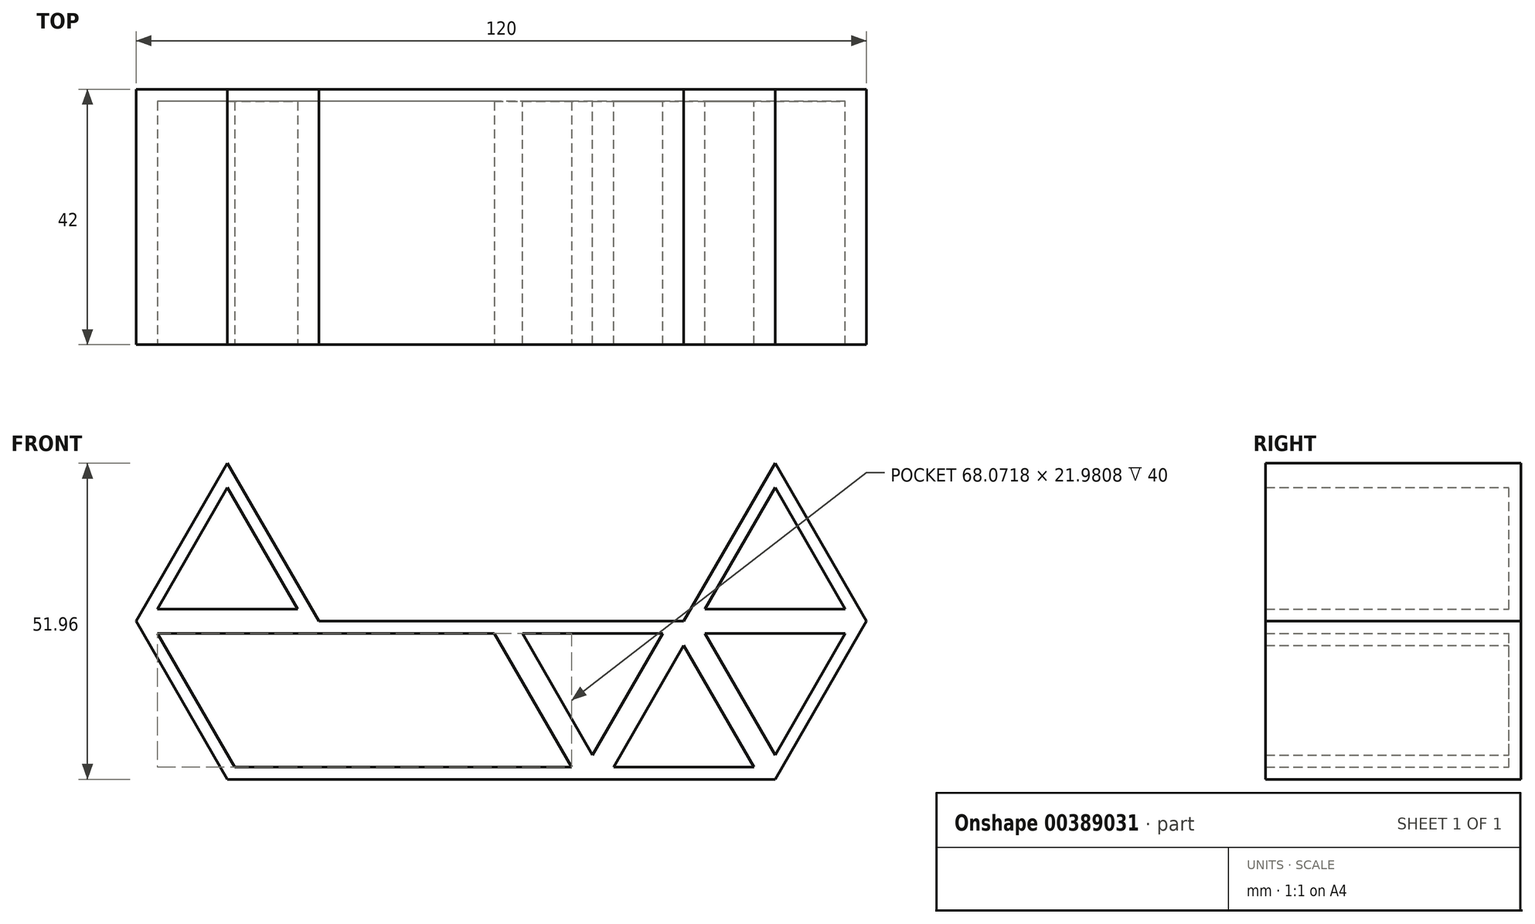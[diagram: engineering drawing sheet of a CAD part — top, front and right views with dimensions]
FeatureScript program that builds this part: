
annotation { "Feature Type Name" : "Feature", "Feature Type Description" : "" }
export const myFeature = defineFeature(function(context is Context, id is Id, definition is map)
    precondition{}
    {
        {
            var Q0;
            Q0=qCreatedBy(makeId("Front.planeOp"),FACE);
            var sketch = newSketch(context, id + "F0", { "sketchPlane" : qUnion([Q0])});
            skCircle(sketch, "E0.cCircle", {"center": v(0, 1.04) * mm, "radius": 8.66 * mm, "construction": true});
            skLineSegment(sketch, "E0.0", {"start": v(15, -7.62) * mm, "end": v(-15, -7.62) * mm});
            skLineSegment(sketch, "E0.1", {"start": v(-15, -7.62) * mm, "end": v(0, 18.36) * mm});
            skLineSegment(sketch, "E0.2", {"start": v(0, 18.36) * mm, "end": v(15, -7.62) * mm});
            skPoint(sketch, "E0.0.midPoint", {"position": v(0, -7.62) * mm});
            skLineSegment(sketch, "E1.0", {"start": v(0, 14.36) * mm, "end": v(11.54, -5.62) * mm});
            skLineSegment(sketch, "E1.1", {"start": v(-11.54, -5.62) * mm, "end": v(0, 14.36) * mm});
            skLineSegment(sketch, "E1.2", {"start": v(11.54, -5.62) * mm, "end": v(-11.54, -5.62) * mm});
            skLineSegment(sketch, "E2.MirrorCS", {"start": v(11.54, -9.62) * mm, "end": v(-11.54, -9.62) * mm});
            skCircle(sketch, "E3.MirrorC", {"center": v(0, -16.28) * mm, "radius": 8.66 * mm, "construction": true});
            skLineSegment(sketch, "E4.MirrorCS", {"start": v(-15, -7.62) * mm, "end": v(0, -33.6) * mm});
            skLineSegment(sketch, "E5.MirrorCS", {"start": v(0, -33.6) * mm, "end": v(15, -7.62) * mm});
            skLineSegment(sketch, "E6.MirrorCS", {"start": v(-11.54, -9.62) * mm, "end": v(0, -29.6) * mm});
            skLineSegment(sketch, "E7.MirrorCS", {"start": v(0, -29.6) * mm, "end": v(11.54, -9.62) * mm});
            skLineSegment(sketch, "E8.1.0.0", {"start": v(-45, -7.62) * mm, "end": v(-30, -33.6) * mm});
            skLineSegment(sketch, "E8.1.0.1", {"start": v(-15, -7.62) * mm, "end": v(-45, -7.62) * mm});
            skLineSegment(sketch, "E8.1.0.2", {"start": v(-30, -33.6) * mm, "end": v(-15, -7.62) * mm});
            skLineSegment(sketch, "E8.direction1", {"start": v(0, -33.6) * mm, "end": v(-30, -33.6) * mm, "construction": true});
            skLineSegment(sketch, "E9.0", {"start": v(-30, -29.6) * mm, "end": v(-18.46, -9.62) * mm});
            skLineSegment(sketch, "E9.1", {"start": v(-41.54, -9.62) * mm, "end": v(-30, -29.6) * mm});
            skLineSegment(sketch, "E9.2", {"start": v(-18.46, -9.62) * mm, "end": v(-41.54, -9.62) * mm});
            skLineSegment(sketch, "E10", {"start": v(-30, -33.6) * mm, "end": v(0, -33.6) * mm});
            skLineSegment(sketch, "E11.0", {"start": v(-26.54, -31.6) * mm, "end": v(-15, -11.62) * mm});
            skLineSegment(sketch, "E11.1", {"start": v(-3.46, -31.6) * mm, "end": v(-26.54, -31.6) * mm});
            skLineSegment(sketch, "E11.2", {"start": v(-15, -11.62) * mm, "end": v(-3.46, -31.6) * mm});
            skSolve(sketch);
        }
        {
            var Q0;
            Q0=makeQuery(id+"F0.imprint","IMPRINT",FACE,{"disambiguationData":[TD([[makeQuery(id+"F0.imprint","IMPRINT",EDGE,{"derivedFrom":sQuery(id+"F0.wireOp",EDGE,"E8.1.0.0")}),1.0]])]});
            var Q1;
            Q1=makeQuery(id+"F0.imprint","IMPRINT",FACE,{"disambiguationData":[TD([[makeQuery(id+"F0.imprint","IMPRINT",EDGE,{"derivedFrom":sQuery(id+"F0.wireOp",EDGE,"E4.MirrorCS")}),-1.0]])]});
            var Q2;
            Q2=makeQuery(id+"F0.imprint","IMPRINT",FACE,{"disambiguationData":[TD([[makeQuery(id+"F0.imprint","IMPRINT",EDGE,{"derivedFrom":sQuery(id+"F0.wireOp",EDGE,"E0.0")}),1.0]])]});
            var Q3;
            Q3=makeQuery(id+"F0.imprint","IMPRINT",FACE,{"disambiguationData":[TD([[makeQuery(id+"F0.imprint","IMPRINT",EDGE,{"derivedFrom":sQuery(id+"F0.wireOp",EDGE,"E0.0")}),-1.0]])]});
            extrude(context, id + "F1", {"entities" : qUnion([Q0, Q1, Q2, Q3]), "depth" : 40 * mm});
        }
        {
            var Q0;
            Q0=makeQuery(id+"F1.opExtrude","CAP_FACE",FACE,{"disambiguationData":[OSD([sQuery(id+"F0.wireOp",EDGE,"E0.1"),sQuery(id+"F0.wireOp",EDGE,"E0.2"),sQuery(id+"F0.wireOp",EDGE,"E1.0"),sQuery(id+"F0.wireOp",EDGE,"E1.1"),sQuery(id+"F0.wireOp",EDGE,"E1.2"),sQuery(id+"F0.wireOp",EDGE,"E2.MirrorCS"),sQuery(id+"F0.wireOp",EDGE,"E5.MirrorCS"),sQuery(id+"F0.wireOp",EDGE,"E6.MirrorCS"),sQuery(id+"F0.wireOp",EDGE,"E7.MirrorCS"),sQuery(id+"F0.wireOp",EDGE,"E8.1.0.0"),sQuery(id+"F0.wireOp",EDGE,"E8.1.0.1"),sQuery(id+"F0.wireOp",EDGE,"E9.0"),sQuery(id+"F0.wireOp",EDGE,"E9.1"),sQuery(id+"F0.wireOp",EDGE,"E9.2"),sQuery(id+"F0.wireOp",EDGE,"E10"),sQuery(id+"F0.wireOp",EDGE,"E11.0"),sQuery(id+"F0.wireOp",EDGE,"E11.1"),sQuery(id+"F0.wireOp",EDGE,"E11.2")])],"isStart":false});
            var sketch = newSketch(context, id + "F2", { "sketchPlane" : qUnion([Q0])});
            skLineSegment(sketch, "E12", {"start": v(-45, -7.62) * mm, "end": v(-75, -7.62) * mm});
            skLineSegment(sketch, "E13", {"start": v(-75, -7.62) * mm, "end": v(-105, -7.62) * mm});
            skLineSegment(sketch, "E14", {"start": v(-30, -33.6) * mm, "end": v(-90, -33.6) * mm});
            skLineSegment(sketch, "E15", {"start": v(-90, -33.6) * mm, "end": v(-105, -7.62) * mm});
            skLineSegment(sketch, "E16.0", {"start": v(-88.85, -31.6) * mm, "end": v(-101.54, -9.62) * mm});
            skLineSegment(sketch, "E16.1", {"start": v(-75, -9.62) * mm, "end": v(-101.54, -9.62) * mm});
            skLineSegment(sketch, "E16.2", {"start": v(-33.46, -31.6) * mm, "end": v(-88.85, -31.6) * mm});
            skLineSegment(sketch, "E16.3", {"start": v(-46.15, -9.62) * mm, "end": v(-33.46, -31.6) * mm});
            skLineSegment(sketch, "E16.4", {"start": v(-46.15, -9.62) * mm, "end": v(-75, -9.62) * mm});
            skSolve(sketch);
        }
        {
            var Q0;
            Q0=makeQuery(id+"F2.imprint","IMPRINT",FACE,{"disambiguationData":[TD([[makeQuery(id+"F2.imprint","IMPRINT",EDGE,{"derivedFrom":sQuery(id+"F2.wireOp",EDGE,"E12")}),1.0]])]});
            extrude(context, id + "F3", {"entities" : qUnion([Q0]), "operationType" : NewBodyOperationType.ADD, "oppositeDirection" : true, "depth" : 40 * mm});
        }
        {
            var Q0;
            {var subQ0=sQuery(id+"F0.wireOp",EDGE,"E8.1.0.0");Q0=makeQuery(id+"F3.boolean.opBoolean","MERGE",FACE,{"derivedFrom":[makeQuery(id+"F1.opExtrude","CAP_FACE",FACE,{"disambiguationData":[OSD([sQuery(id+"F0.wireOp",EDGE,"E0.1"),sQuery(id+"F0.wireOp",EDGE,"E0.2"),sQuery(id+"F0.wireOp",EDGE,"E1.0"),sQuery(id+"F0.wireOp",EDGE,"E1.1"),sQuery(id+"F0.wireOp",EDGE,"E1.2"),sQuery(id+"F0.wireOp",EDGE,"E2.MirrorCS"),sQuery(id+"F0.wireOp",EDGE,"E5.MirrorCS"),sQuery(id+"F0.wireOp",EDGE,"E6.MirrorCS"),sQuery(id+"F0.wireOp",EDGE,"E7.MirrorCS"),subQ0,sQuery(id+"F0.wireOp",EDGE,"E8.1.0.1"),sQuery(id+"F0.wireOp",EDGE,"E9.0"),sQuery(id+"F0.wireOp",EDGE,"E9.1"),sQuery(id+"F0.wireOp",EDGE,"E9.2"),sQuery(id+"F0.wireOp",EDGE,"E10"),sQuery(id+"F0.wireOp",EDGE,"E11.0"),sQuery(id+"F0.wireOp",EDGE,"E11.1"),sQuery(id+"F0.wireOp",EDGE,"E11.2")])],"isStart":false}),makeQuery(id+"F3.opExtrude","CAP_FACE",FACE,{"disambiguationData":[OSD([subQ0,sQuery(id+"F2.wireOp",EDGE,"E12"),sQuery(id+"F2.wireOp",EDGE,"E13"),sQuery(id+"F2.wireOp",EDGE,"E14"),sQuery(id+"F2.wireOp",EDGE,"E15"),sQuery(id+"F2.wireOp",EDGE,"E16.0"),sQuery(id+"F2.wireOp",EDGE,"E16.1"),sQuery(id+"F2.wireOp",EDGE,"E16.2"),sQuery(id+"F2.wireOp",EDGE,"E16.3"),sQuery(id+"F2.wireOp",EDGE,"E16.4")])],"isStart":true})]});}
            var sketch = newSketch(context, id + "F4", { "sketchPlane" : qUnion([Q0])});
            skLineSegment(sketch, "E17", {"start": v(-105, -7.62) * mm, "end": v(-90, -7.62) * mm, "construction": true});
            skLineSegment(sketch, "E18", {"start": v(-90, -7.62) * mm, "end": v(-90, 18.36) * mm, "construction": true});
            skLineSegment(sketch, "E19", {"start": v(-90, 18.36) * mm, "end": v(-105, -7.62) * mm});
            skLineSegment(sketch, "E20.MirrorCS", {"start": v(-90, 18.36) * mm, "end": v(-75, -7.62) * mm});
            skLineSegment(sketch, "E21.MirrorCS", {"start": v(-75, -7.62) * mm, "end": v(-90, -7.62) * mm, "construction": true});
            skLineSegment(sketch, "E22.0", {"start": v(-90, 14.36) * mm, "end": v(-78.46, -5.62) * mm});
            skLineSegment(sketch, "E22.1", {"start": v(-90, 14.36) * mm, "end": v(-101.54, -5.62) * mm});
            skLineSegment(sketch, "E22.2", {"start": v(-101.54, -5.62) * mm, "end": v(-90, -5.62) * mm});
            skLineSegment(sketch, "E22.3", {"start": v(-78.46, -5.62) * mm, "end": v(-90, -5.62) * mm});
            skSolve(sketch);
        }
        {
            var Q0;
            {var subQ1=sQuery(id+"F4.wireOp",EDGE,"E19");Q0=makeQuery(id+"F4.imprint","IMPRINT",FACE,{"disambiguationData":[TD([[makeQuery(id+"F4.imprint","IMPRINT",EDGE,{"derivedFrom":subQ1}),1.0]])]});}
            extrude(context, id + "F5", {"entities" : qUnion([Q0]), "operationType" : NewBodyOperationType.ADD, "oppositeDirection" : true, "depth" : 40 * mm});
        }
        {
            var Q0;
            {var subQ0=sQuery(id+"F2.wireOp",EDGE,"E13");var subQ1=sQuery(id+"F2.wireOp",EDGE,"E12");var subQ2=sQuery(id+"F0.wireOp",EDGE,"E8.1.0.1");var subQ3=sQuery(id+"F0.wireOp",EDGE,"E8.1.0.0");Q0=makeQuery(id+"F5.boolean.opBoolean","MERGE",FACE,{"derivedFrom":[makeQuery(id+"F3.boolean.opBoolean","MERGE",FACE,{"derivedFrom":[makeQuery(id+"F1.opExtrude","CAP_FACE",FACE,{"disambiguationData":[OSD([sQuery(id+"F0.wireOp",EDGE,"E0.1"),sQuery(id+"F0.wireOp",EDGE,"E0.2"),sQuery(id+"F0.wireOp",EDGE,"E1.0"),sQuery(id+"F0.wireOp",EDGE,"E1.1"),sQuery(id+"F0.wireOp",EDGE,"E1.2"),sQuery(id+"F0.wireOp",EDGE,"E2.MirrorCS"),sQuery(id+"F0.wireOp",EDGE,"E5.MirrorCS"),sQuery(id+"F0.wireOp",EDGE,"E6.MirrorCS"),sQuery(id+"F0.wireOp",EDGE,"E7.MirrorCS"),subQ3,subQ2,sQuery(id+"F0.wireOp",EDGE,"E9.0"),sQuery(id+"F0.wireOp",EDGE,"E9.1"),sQuery(id+"F0.wireOp",EDGE,"E9.2"),sQuery(id+"F0.wireOp",EDGE,"E10"),sQuery(id+"F0.wireOp",EDGE,"E11.0"),sQuery(id+"F0.wireOp",EDGE,"E11.1"),sQuery(id+"F0.wireOp",EDGE,"E11.2")])],"isStart":true}),makeQuery(id+"F3.opExtrude","CAP_FACE",FACE,{"disambiguationData":[OSD([subQ3,subQ1,subQ0,sQuery(id+"F2.wireOp",EDGE,"E14"),sQuery(id+"F2.wireOp",EDGE,"E15"),sQuery(id+"F2.wireOp",EDGE,"E16.0"),sQuery(id+"F2.wireOp",EDGE,"E16.1"),sQuery(id+"F2.wireOp",EDGE,"E16.2"),sQuery(id+"F2.wireOp",EDGE,"E16.3"),sQuery(id+"F2.wireOp",EDGE,"E16.4")])],"isStart":false})]}),makeQuery(id+"F5.opExtrude","CAP_FACE",FACE,{"disambiguationData":[OSD([subQ2,subQ1,subQ0,sQuery(id+"F4.wireOp",EDGE,"E19"),sQuery(id+"F4.wireOp",EDGE,"E20.MirrorCS"),sQuery(id+"F4.wireOp",EDGE,"E22.0"),sQuery(id+"F4.wireOp",EDGE,"E22.1"),sQuery(id+"F4.wireOp",EDGE,"E22.2"),sQuery(id+"F4.wireOp",EDGE,"E22.3")])],"isStart":false})]});}
            var sketch = newSketch(context, id + "F6", { "sketchPlane" : qUnion([Q0])});
            skLineSegment(sketch, "E23.0", {"start": v(-15, -7.62) * mm, "end": v(0, -33.6) * mm});
            skLineSegment(sketch, "E23.1", {"start": v(0, 18.36) * mm, "end": v(-15, -7.62) * mm});
            skLineSegment(sketch, "E23.2", {"start": v(0, -33.6) * mm, "end": v(90, -33.6) * mm});
            skLineSegment(sketch, "E23.3", {"start": v(15, -7.62) * mm, "end": v(0, 18.36) * mm});
            skLineSegment(sketch, "E23.4", {"start": v(90, -33.6) * mm, "end": v(105, -7.62) * mm});
            skLineSegment(sketch, "E23.5", {"start": v(105, -7.62) * mm, "end": v(90, 18.36) * mm});
            skLineSegment(sketch, "E23.6", {"start": v(90, 18.36) * mm, "end": v(75, -7.62) * mm});
            skLineSegment(sketch, "E23.7", {"start": v(75, -7.62) * mm, "end": v(15, -7.62) * mm});
            skSolve(sketch);
        }
        {
            var Q0;
            Q0 = qSketchRegion(id + "F6", true);
            extrude(context, id + "F7", {"entities" : qUnion([Q0]), "operationType" : NewBodyOperationType.ADD, "depth" : 2 * mm});
        }
    });
